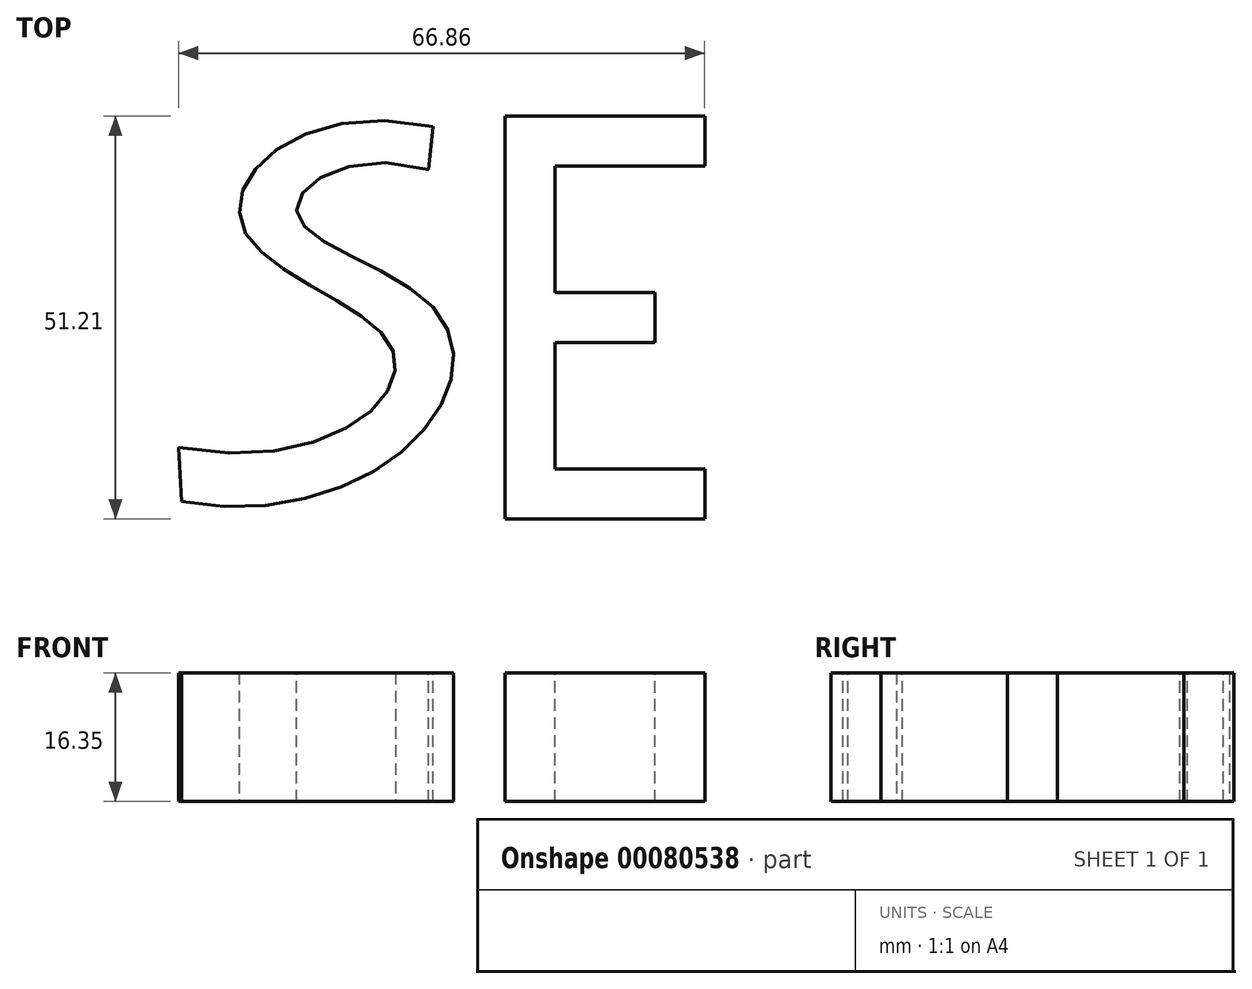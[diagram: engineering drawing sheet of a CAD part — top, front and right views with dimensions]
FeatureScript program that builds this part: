
annotation { "Feature Type Name" : "Feature", "Feature Type Description" : "" }
export const myFeature = defineFeature(function(context is Context, id is Id, definition is map)
    precondition{}
    {
        {
            var Q0;
            Q0=qCreatedBy(makeId("Top.planeOp"),FACE);
            var sketch = newSketch(context, id + "F0", { "sketchPlane" : qUnion([Q0])});
            skFitSpline(sketch, "E0", {"points": [v(-6.35, 10.36) * mm, v(-23.06, 4.62) * mm, v(-5.88, -6.98) * mm, v(-6.55, -22.2) * mm, v(-37.74, -31.8) * mm], "startDerivative": vector(-132.72, 38.76) * mm, "endDerivative": vector(-125.71, 24.1) * mm});
            skFitSpline(sketch, "E1", {"points": [v(-5.77, 15.85) * mm, v(-29.99, 3.09) * mm, v(-10.9, -12.57) * mm, v(-38.15, -24.95) * mm], "startDerivative": vector(-150.24, 31.5) * mm, "endDerivative": vector(-154.6, 28.92) * mm});
            skLineSegment(sketch, "E2", {"start": v(-5.77, 15.85) * mm, "end": v(-6.35, 10.36) * mm});
            skLineSegment(sketch, "E3", {"start": v(-38.15, -24.95) * mm, "end": v(-37.74, -31.8) * mm});
            skLineSegment(sketch, "E4.bottom", {"start": v(3.31, 17.18) * mm, "end": v(9.66, 17.18) * mm});
            skLineSegment(sketch, "E4.top", {"start": v(3.31, -34.03) * mm, "end": v(9.66, -34.03) * mm});
            skLineSegment(sketch, "E4.left", {"start": v(3.31, 17.18) * mm, "end": v(3.31, -34.03) * mm});
            skLineSegment(sketch, "E4.right", {"start": v(9.66, 17.18) * mm, "end": v(9.66, -34.03) * mm});
            skLineSegment(sketch, "E5.bottom", {"start": v(9.66, -34.03) * mm, "end": v(28.71, -34.03) * mm});
            skLineSegment(sketch, "E5.top", {"start": v(9.66, -27.68) * mm, "end": v(28.71, -27.68) * mm});
            skLineSegment(sketch, "E5.left", {"start": v(9.66, -34.03) * mm, "end": v(9.66, -27.68) * mm});
            skLineSegment(sketch, "E5.right", {"start": v(28.71, -34.03) * mm, "end": v(28.71, -27.68) * mm});
            skLineSegment(sketch, "E6.bottom", {"start": v(9.66, -11.6) * mm, "end": v(22.36, -11.6) * mm});
            skLineSegment(sketch, "E6.top", {"start": v(9.66, -5.25) * mm, "end": v(22.36, -5.25) * mm});
            skLineSegment(sketch, "E6.left", {"start": v(9.66, -11.6) * mm, "end": v(9.66, -5.25) * mm});
            skLineSegment(sketch, "E6.right", {"start": v(22.36, -11.6) * mm, "end": v(22.36, -5.25) * mm});
            skLineSegment(sketch, "E7.bottom", {"start": v(9.66, 17.18) * mm, "end": v(28.71, 17.18) * mm});
            skLineSegment(sketch, "E7.top", {"start": v(9.66, 10.83) * mm, "end": v(28.71, 10.83) * mm});
            skLineSegment(sketch, "E7.left", {"start": v(9.66, 17.18) * mm, "end": v(9.66, 10.83) * mm});
            skLineSegment(sketch, "E7.right", {"start": v(28.71, 17.18) * mm, "end": v(28.71, 10.83) * mm});
            skSolve(sketch);
        }
        {
            var Q0;
            Q0 = qSketchRegion(id + "F0", true);
            extrude(context, id + "F1", {"entities" : qUnion([Q0]), "oppositeDirection" : true, "depth" : 16.35 * mm});
        }
    });
